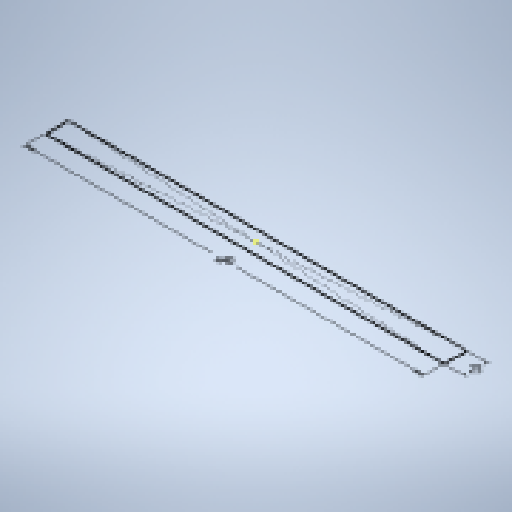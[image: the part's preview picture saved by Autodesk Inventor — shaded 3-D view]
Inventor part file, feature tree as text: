
AUTODESK INVENTOR PART (.ipt)
format: ipt  version: 2024.2 (Build 282272000, 272)  size: 138,240 bytes
history: native  units: mm
features: extrude x1, sketch x1
ambient origin geometry x8: Origin, YZ Plane, XZ Plane, XY Plane, X Axis, Y Axis, Z Axis, Center Point
bodies: Solid1 (feature_tree)
feature tree (2):
  extrude  "Extrusion1"  Depth=25.0mm
  sketch  "Sketch1"  dims[d0=440.0mm d1=25.0mm d2=10.0mm d3=0.0mm]
